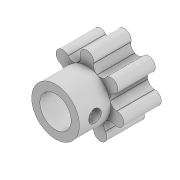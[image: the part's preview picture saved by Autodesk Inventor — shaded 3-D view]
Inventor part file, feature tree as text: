
AUTODESK INVENTOR PART (.ipt)
format: ipt  version: 2020 (Build 240168000, 168)  size: 208,896 bytes
history: native  units: in
note: dims shown in document units (in); Inventor stores cm internally (conversion verified against a paired STEP export)
features: extrude x3, sketch x3
ambient origin geometry x8: Origin, YZ Plane, XZ Plane, XY Plane, X Axis, Y Axis, Z Axis, Center Point
bodies: Solid1 (feature_tree)
feature tree (6):
  extrude  "Extrusion1"  Depth=0.1969in
  extrude  "Extrusion2"  Depth=0.084in
  extrude  "Extrusion3"  Depth=0.1969in
  sketch  "Sketch1"  dims[d0=0.1969in d1=0.4724in]
  sketch  "Sketch2"  dims[d2=0.0866in d5=0.084in]
  sketch  "Sketch3"  dims[d6=0.084in d7=0.084in d8=2.7559in d10=360.0deg d12=0.2362in d13=0.0in d14=0.1969in d15=0.0in d16=0.0787in d17=0.1575in d18=0.0in]
